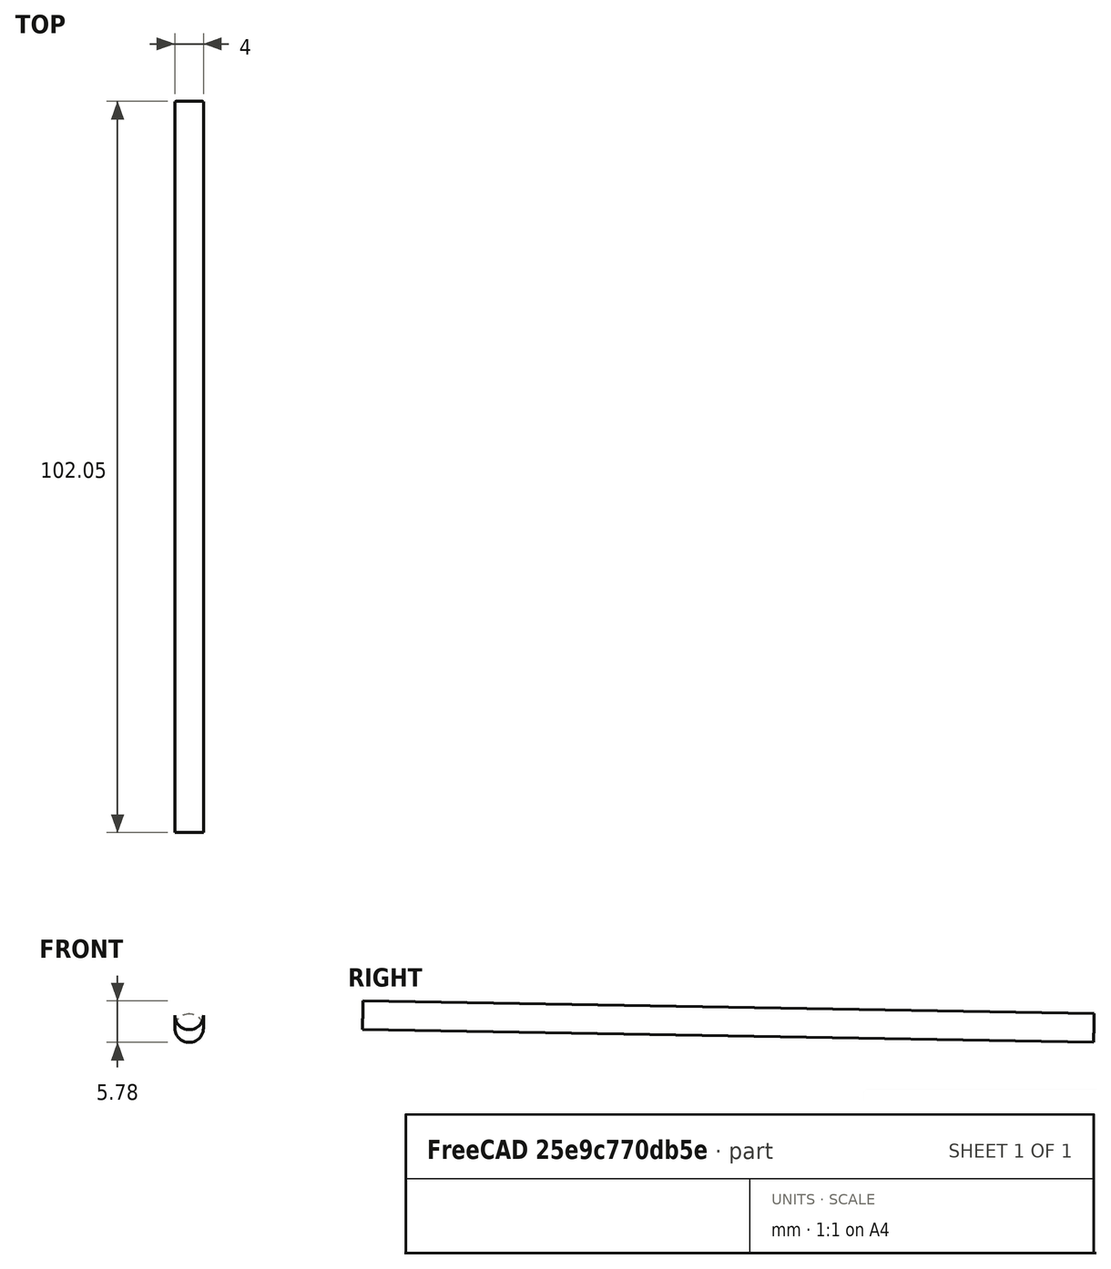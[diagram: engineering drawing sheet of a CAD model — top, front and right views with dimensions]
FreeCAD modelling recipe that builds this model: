
FCSTD DOCUMENT  (FreeCAD 0.20R29410 (Git))
Label: wingtest2
License: All rights reserved
LicenseURL: http://en.wikipedia.org/wiki/All_rights_reserved
objects: Part::Box×16, Part::Cut×13, Part::Part2DObjectPython×10, Part::FeaturePython×5, Part::Cylinder×1
note: 45 computed .brp shape members not serialized (recipe doc carries the construction recipe); baked Part::Feature solids carry a one-line shape summary decoded from their .brp

FEATURE [Part::FeaturePython] wrib  # WARN: FeaturePython — macro-defined, semantics opaque (R4)
  Chord = 200
  Coordinates = (101) [(1,0,-1.66493e-17),(0.99901,0,0.000165069),(0.996045,0,0.00065853),(0.991115,0,0.00147518),(0.984242,0,0.00260652),(0.975451,0,0.00404094),+95 more]
  NacaNbrPoint = 50
  NacaProfil = 23012
  RibProfil = 23012
  Thickness = 0
  finite_TE = false
  splitSpline = true
  useSpline = true
  wingkey = 0
FEATURE [Part::FeaturePython] wrib001  label="wrib175"  # WARN: FeaturePython — macro-defined, semantics opaque (R4)
  Chord = 175
  Coordinates = (101) [(1,0,-1.66493e-17),(0.99901,0,0.000165069),(0.996045,0,0.00065853),(0.991115,0,0.00147518),(0.984242,0,0.00260652),(0.975451,0,0.00404094),+95 more]
  NacaNbrPoint = 50
  NacaProfil = 23012
  Placement = pos=(25,-25,0) rot=(1,0,0;0rad)
  RibProfil = 23012
  Thickness = 0
  finite_TE = false
  splitSpline = true
  useSpline = true
  wingkey = 0
FEATURE [Part::FeaturePython] wrib002  label="wrib150"  # WARN: FeaturePython — macro-defined, semantics opaque (R4)
  Chord = 150
  Coordinates = (101) [(1,0,-1.66493e-17),(0.99901,0,0.000165069),(0.996045,0,0.00065853),(0.991115,0,0.00147518),(0.984242,0,0.00260652),(0.975451,0,0.00404094),+95 more]
  NacaNbrPoint = 50
  NacaProfil = 23012
  Placement = pos=(50,-50,0) rot=(1,0,0;0rad)
  RibProfil = 23012
  Thickness = 0
  finite_TE = false
  splitSpline = true
  useSpline = true
  wingkey = 0
FEATURE [Part::FeaturePython] wrib003  label="wrib125"  # WARN: FeaturePython — macro-defined, semantics opaque (R4)
  Chord = 125
  Coordinates = (101) [(1,0,-1.66493e-17),(0.99901,0,0.000165069),(0.996045,0,0.00065853),(0.991115,0,0.00147518),(0.984242,0,0.00260652),(0.975451,0,0.00404094),+95 more]
  NacaNbrPoint = 50
  NacaProfil = 23012
  Placement = pos=(75,-75,0) rot=(1,0,0;0rad)
  RibProfil = 23012
  Thickness = 0
  finite_TE = false
  splitSpline = true
  useSpline = true
  wingkey = 0
FEATURE [Part::FeaturePython] wrib004  label="wrib100"  # WARN: FeaturePython — macro-defined, semantics opaque (R4)
  Chord = 100
  Coordinates = (101) [(1,0,-1.66493e-17),(0.99901,0,0.000165069),(0.996045,0,0.00065853),(0.991115,0,0.00147518),(0.984242,0,0.00260652),(0.975451,0,0.00404094),+95 more]
  NacaNbrPoint = 50
  NacaProfil = 23012
  Placement = pos=(100,-100,0) rot=(1,0,0;0rad)
  RibProfil = 23012
  Thickness = 0
  finite_TE = false
  splitSpline = true
  useSpline = true
  wingkey = 0
FEATURE [Part::Box] Box001  label="Cube001"
  AttacherType = Attacher::AttachEngine3D
  Height = 4.5
  Length = 10
  Placement = pos=(113,-101,-1) rot=(0,0,1;0rad)
  Width = 110
FEATURE [Part::Box] Box002  label="Cube002"
  AttacherType = Attacher::AttachEngine3D
  Height = 4.5
  Length = 10
  Placement = pos=(113,-101,-1) rot=(0,0,1;0rad)
  Width = 110
FEATURE [Part::Box] Box003  label="Cube003"
  AttacherType = Attacher::AttachEngine3D
  Height = 4.5
  Length = 10
  Placement = pos=(113,-101,-1) rot=(0,0,1;0rad)
  Width = 110
FEATURE [Part::Box] Box004  label="Cube004"
  AttacherType = Attacher::AttachEngine3D
  Height = 4.5
  Length = 10
  Placement = pos=(113,-101,-1) rot=(0,0,1;0rad)
  Width = 110
FEATURE [Part::Box] Box005  label="Cube005"
  AttacherType = Attacher::AttachEngine3D
  Height = 4.5
  Length = 10
  Placement = pos=(113,-101,-1) rot=(0,0,1;0rad)
  Width = 110
FEATURE [Part::Box] Box006  label="spar1"
  AttacherType = Attacher::AttachEngine3D
  Height = 4.5
  Length = 10
  Placement = pos=(113,-104.7,-1) rot=(0,0,1;0rad)
  Width = 110
FEATURE [Part::Cut] Cut  label="little_wing"
  Base = -> wrib004
  Tool = -> Box002
FEATURE [Part::Cut] Cut001  label="wing_04"
  Base = -> wrib003
  Tool = -> Box001
FEATURE [Part::Cut] Cut002  label="wing_03"
  Base = -> wrib002
  Tool = -> Box003
FEATURE [Part::Cut] Cut003  label="wing_02"
  Base = -> wrib001
  Tool = -> Box004
FEATURE [Part::Cut] Cut004  label="big_wing"
  Base = -> wrib
  Tool = -> Box005
FEATURE [Part::Box] Box007  label="spar2"
  AttacherType = Attacher::AttachEngine3D
  Height = 4.5
  Length = 10
  Placement = pos=(84.6,-79.4,-1) rot=(0,0,1;0rad)
  Width = 89
FEATURE [Part::Box] Box008  label="spar003"
  AttacherType = Attacher::AttachEngine3D
  Height = 4.5
  Length = 10
  Placement = pos=(84.6,-79.4,-1) rot=(0,0,1;0rad)
  Width = 89
FEATURE [Part::Box] Box009  label="spar004"
  AttacherType = Attacher::AttachEngine3D
  Height = 4.5
  Length = 10
  Placement = pos=(84.6,-79.4,-1) rot=(0,0,1;0rad)
  Width = 89
FEATURE [Part::Box] Box010  label="spar005"
  AttacherType = Attacher::AttachEngine3D
  Height = 4.5
  Length = 10
  Placement = pos=(84.6,-79.4,-1) rot=(0,0,1;0rad)
  Width = 89
FEATURE [Part::Cut] Cut005
  Base = -> Cut001
  Tool = -> Box008
FEATURE [Part::Cut] Cut007
  Base = -> Cut003
  Tool = -> Box010
FEATURE [Part::Box] Box011  label="spar006"
  AttacherType = Attacher::AttachEngine3D
  Height = 4.5
  Length = 10
  Placement = pos=(84.6,-79.4,-1) rot=(0,0,1;0rad)
  Width = 89
FEATURE [Part::Cut] Cut008
  Base = -> Cut002
  Tool = -> Box011
FEATURE [Part::Box] Box012  label="spar007"
  AttacherType = Attacher::AttachEngine3D
  Height = 4.5
  Length = 10
  Placement = pos=(84.6,-79.4,-1) rot=(0,0,1;0rad)
  Width = 89
FEATURE [Part::Cut] Cut009
  Base = -> Cut
  Tool = -> Box012
FEATURE [Part::Box] Box013  label="spar3"
  AttacherType = Attacher::AttachEngine3D
  Height = 4.5
  Length = 10
  Placement = pos=(62.5,-59.2,-1) rot=(0,0,1;0rad)
  Width = 66
FEATURE [Part::Box] Box014  label="spar008"
  AttacherType = Attacher::AttachEngine3D
  Height = 4.5
  Length = 10
  Placement = pos=(62.5,-56,-1) rot=(0,0,1;0rad)
  Width = 66
FEATURE [Part::Box] Box015  label="spar009"
  AttacherType = Attacher::AttachEngine3D
  Height = 4.5
  Length = 10
  Placement = pos=(62.5,-56,-1) rot=(0,0,1;0rad)
  Width = 66
FEATURE [Part::Cut] Cut010
  Base = -> Cut008
  Tool = -> Box014
FEATURE [Part::Cut] Cut011
  Base = -> Cut007
  Tool = -> Box015
FEATURE [Part::Cut] Cut006
  Base = -> Cut004
  Tool = -> Box009
FEATURE [Part::Box] Box016  label="spar010"
  AttacherType = Attacher::AttachEngine3D
  Height = 4.5
  Length = 10
  Placement = pos=(62.5,-56,-1) rot=(0,0,1;0rad)
  Width = 66
FEATURE [Part::Cut] Cut012
  Base = -> Cut006
  Tool = -> Box016
FEATURE [Part::Part2DObjectPython] Shape2DView001  # Draft 2D object (typed FeaturePython)
  AutoUpdate = true
  Base = -> Box013
  Clip = false
  FuseArch = false
  HiddenLines = false
  InPlace = true
  OnlySolids = false
  Placement = pos=(-143.662,128.214,0) rot=(0,0,1;0rad)
  Projection = (-6.95423e-07,2.08616e-07,1)
  ProjectionMode = 0
  SegmentLength = 0.05
  Tessellation = false
  VisibleOnly = false
FEATURE [Part::Part2DObjectPython] Shape2DView002  # Draft 2D object (typed FeaturePython)
  AutoUpdate = true
  Base = -> Box007
  Clip = false
  FuseArch = false
  HiddenLines = false
  InPlace = true
  OnlySolids = false
  Placement = pos=(-116.371,128.729,0) rot=(0,0,1;0rad)
  Projection = (-6.95423e-07,2.08616e-07,1)
  ProjectionMode = 0
  SegmentLength = 0.05
  Tessellation = false
  VisibleOnly = false
FEATURE [Part::Part2DObjectPython] Shape2DView003  # Draft 2D object (typed FeaturePython)
  AutoUpdate = true
  Base = -> Box006
  Clip = false
  FuseArch = false
  HiddenLines = false
  InPlace = true
  OnlySolids = false
  Placement = pos=(-116.371,128.729,0) rot=(0,0,1;0rad)
  Projection = (-6.95423e-07,2.08616e-07,1)
  ProjectionMode = 0
  SegmentLength = 0.05
  Tessellation = false
  VisibleOnly = false
FEATURE [Part::Part2DObjectPython] Shape2DView004  # Draft 2D object (typed FeaturePython)
  AutoUpdate = true
  Base = -> Cut005
  Clip = false
  FuseArch = false
  HiddenLines = false
  InPlace = true
  OnlySolids = false
  Placement = pos=(-99.379,-300.711,0) rot=(0,0,1;0rad)
  Projection = (2.68221e-07,1,-3.8743e-07)
  ProjectionMode = 0
  SegmentLength = 0.05
  Tessellation = false
  VisibleOnly = false
FEATURE [Part::Part2DObjectPython] Shape2DView005  # Draft 2D object (typed FeaturePython)
  AutoUpdate = true
  Base = -> Cut009
  Clip = false
  FuseArch = false
  HiddenLines = false
  InPlace = true
  OnlySolids = false
  Placement = pos=(-124.61,-327.487,0) rot=(0,0,1;0rad)
  Projection = (2.68221e-07,1,-3.8743e-07)
  ProjectionMode = 0
  SegmentLength = 0.05
  Tessellation = false
  VisibleOnly = false
FEATURE [Part::Part2DObjectPython] Shape2DView006  # Draft 2D object (typed FeaturePython)
  AutoUpdate = true
  Base = -> Cut010
  Clip = false
  FuseArch = false
  HiddenLines = false
  InPlace = true
  OnlySolids = false
  Placement = pos=(-70.5436,-275.995,0) rot=(0,0,1;0rad)
  Projection = (2.68221e-07,1,-3.8743e-07)
  ProjectionMode = 0
  SegmentLength = 0.05
  Tessellation = false
  VisibleOnly = false
FEATURE [Part::Part2DObjectPython] Shape2DView007  # Draft 2D object (typed FeaturePython)
  AutoUpdate = true
  Base = -> Cut011
  Clip = false
  FuseArch = false
  HiddenLines = false
  InPlace = true
  OnlySolids = false
  Placement = pos=(-42.2232,-249.22,0) rot=(0,0,1;0rad)
  Projection = (2.68221e-07,1,-3.8743e-07)
  ProjectionMode = 0
  SegmentLength = 0.05
  Tessellation = false
  VisibleOnly = false
FEATURE [Part::Part2DObjectPython] Shape2DView008  # Draft 2D object (typed FeaturePython)
  AutoUpdate = true
  Base = -> Cut012
  Clip = false
  FuseArch = false
  HiddenLines = false
  InPlace = true
  OnlySolids = false
  Placement = pos=(-8.75361,-225.534,0) rot=(0,0,1;0rad)
  Projection = (2.68221e-07,1,-3.8743e-07)
  ProjectionMode = 0
  SegmentLength = 0.05
  Tessellation = false
  VisibleOnly = false
FEATURE [Part::Part2DObjectPython] BSpline  # Draft 2D object (typed FeaturePython)
  Area = 0
  Closed = false
  MakeFace = true
  Parameterization = 1
  Points = (3) [(-36.4405,-86.0759,0),(-42.3337,-91.1518,0),(-46.0032,-86.7136,0)]
FEATURE [Part::Part2DObjectPython] BSpline001  # Draft 2D object (typed FeaturePython)
  Area = 0
  Closed = false
  MakeFace = true
  Parameterization = 1
  Points = (3) [(-65.6921,-105.822,0),(-69.5266,-110.292,0),(-73.3485,-106.801,0)]
FEATURE [Part::Cylinder] Cylinder
  Angle = 360
  AttacherType = Attacher::AttachEngine3D
  FirstAngle = 0
  Height = 102
  Placement = pos=(158.9,-98.585,1.72081) rot=(1,0,0;4.69494rad)
  Radius = 2
  SecondAngle = 0
